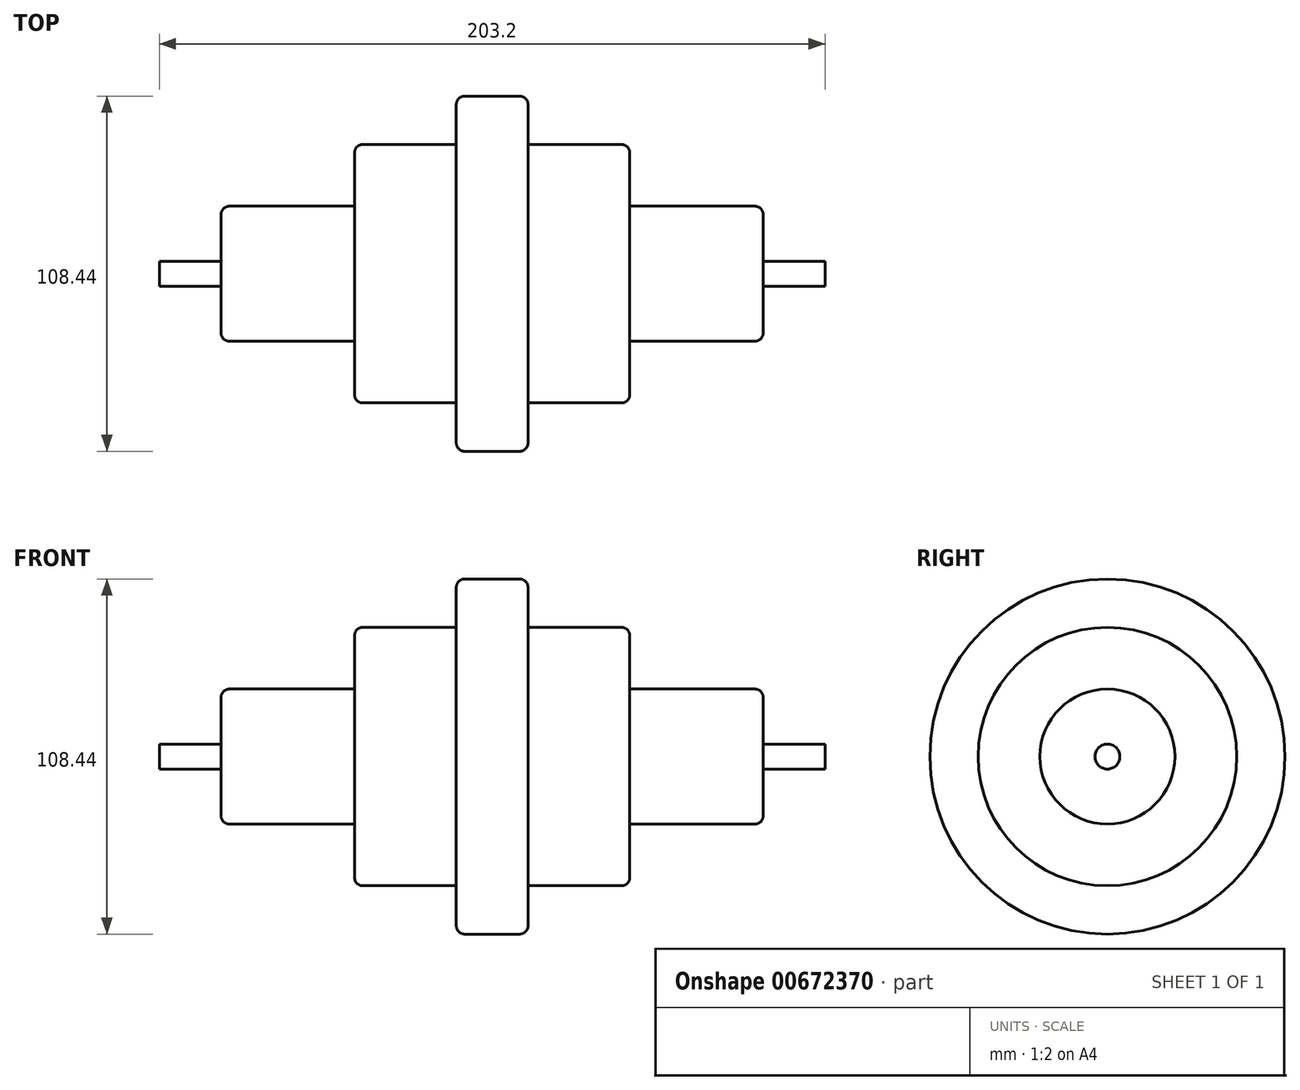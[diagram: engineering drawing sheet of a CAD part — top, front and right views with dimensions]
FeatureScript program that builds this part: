
annotation { "Feature Type Name" : "Feature", "Feature Type Description" : "" }
export const myFeature = defineFeature(function(context is Context, id is Id, definition is map)
    precondition{}
    {
        {
            var Q0;
            Q0=qCreatedBy(makeId("Right.planeOp"),FACE);
            var sketch = newSketch(context, id + "F0", { "sketchPlane" : qUnion([Q0])});
            skCircle(sketch, "E0", {"center": v(0, 0) * mm, "radius": 3.81 * mm});
            skSolve(sketch);
        }
        {
            var Q0;
            Q0=makeQuery(id+"F0.imprint","IMPRINT",FACE,{"disambiguationData":[TD([[makeQuery(id+"F0.imprint","IMPRINT",EDGE,{"derivedFrom":sQuery(id+"F0.wireOp",EDGE,"E0")}),1.0]])]});
            extrude(context, id + "F1", {"entities" : qUnion([Q0]), "endBound" : BoundingType.SYMMETRIC, "depth" : 203.2 * mm, "offsetDistance" : 25.4 * mm});
        }
        {
            var Q0;
            Q0=qCreatedBy(makeId("Front.planeOp"),FACE);
            var sketch = newSketch(context, id + "F2", { "sketchPlane" : qUnion([Q0])});
            skLineSegment(sketch, "E1", {"start": v(0, 0) * mm, "end": v(0, 54.22) * mm, "construction": true});
            skLineSegment(sketch, "E2", {"start": v(-82.74, 0) * mm, "end": v(-82.74, 20.62) * mm});
            skLineSegment(sketch, "E3", {"start": v(-82.74, 20.62) * mm, "end": v(-42, 20.62) * mm});
            skLineSegment(sketch, "E4", {"start": v(-42, 20.62) * mm, "end": v(-42, 39.46) * mm});
            skLineSegment(sketch, "E5", {"start": v(-42, 39.46) * mm, "end": v(-10.95, 39.46) * mm});
            skLineSegment(sketch, "E6", {"start": v(-10.95, 39.46) * mm, "end": v(-10.95, 54.22) * mm});
            skLineSegment(sketch, "E7", {"start": v(-10.95, 54.22) * mm, "end": v(0, 54.22) * mm});
            skLineSegment(sketch, "E8.MirrorCS", {"start": v(10.95, 54.22) * mm, "end": v(0, 54.22) * mm});
            skLineSegment(sketch, "E9.MirrorCS", {"start": v(82.74, 20.62) * mm, "end": v(42, 20.62) * mm});
            skLineSegment(sketch, "E10.MirrorCS", {"start": v(42, 39.46) * mm, "end": v(10.95, 39.46) * mm});
            skLineSegment(sketch, "E11.MirrorCS", {"start": v(82.74, 0) * mm, "end": v(82.74, 20.62) * mm});
            skLineSegment(sketch, "E12.MirrorCS", {"start": v(42, 20.62) * mm, "end": v(42, 39.46) * mm});
            skLineSegment(sketch, "E13.MirrorCS", {"start": v(10.95, 39.46) * mm, "end": v(10.95, 54.22) * mm});
            skLineSegment(sketch, "E14", {"start": v(-82.74, 0) * mm, "end": v(82.74, 0) * mm});
            skSolve(sketch);
        }
        {
            var Q0;
            Q0=makeQuery(id+"F2.imprint","IMPRINT",FACE,{"disambiguationData":[TD([[makeQuery(id+"F2.imprint","IMPRINT",EDGE,{"derivedFrom":sQuery(id+"F2.wireOp",EDGE,"E2")}),-1.0]])]});
            var Q1;
            Q1=sQuery(id+"F2.wireOp",EDGE,"E14");
            revolve(context, id + "F3", {"operationType" : NewBodyOperationType.ADD, "entities" : qUnion([Q0]), "axis" : qUnion([Q1]), "revolveType" : RevolveType.FULL});
        }
        {
            var Q0;
            Q0=makeQuery(id+"F3.opRevolve","SWEPT_EDGE",EDGE,{"disambiguationData":[OSD([sQuery(id+"F2.wireOp",EDGE,"E6"),sQuery(id+"F2.wireOp",EDGE,"E7")])]});
            var Q1;
            Q1=makeQuery(id+"F3.opRevolve","SWEPT_EDGE",EDGE,{"disambiguationData":[OSD([sQuery(id+"F2.wireOp",EDGE,"E4"),sQuery(id+"F2.wireOp",EDGE,"E5")])]});
            var Q2;
            Q2=makeQuery(id+"F3.opRevolve","SWEPT_EDGE",EDGE,{"disambiguationData":[OSD([sQuery(id+"F2.wireOp",EDGE,"E2"),sQuery(id+"F2.wireOp",EDGE,"E3")])]});
            var Q3;
            Q3=makeQuery(id+"F3.opRevolve","SWEPT_EDGE",EDGE,{"disambiguationData":[OSD([sQuery(id+"F2.wireOp",EDGE,"E8.MirrorCS"),sQuery(id+"F2.wireOp",EDGE,"E13.MirrorCS")])]});
            var Q4;
            Q4=makeQuery(id+"F3.opRevolve","SWEPT_EDGE",EDGE,{"disambiguationData":[OSD([sQuery(id+"F2.wireOp",EDGE,"E10.MirrorCS"),sQuery(id+"F2.wireOp",EDGE,"E12.MirrorCS")])]});
            var Q5;
            Q5=makeQuery(id+"F3.opRevolve","SWEPT_EDGE",EDGE,{"disambiguationData":[OSD([sQuery(id+"F2.wireOp",EDGE,"E9.MirrorCS"),sQuery(id+"F2.wireOp",EDGE,"E11.MirrorCS")])]});
            fillet(context, id + "F4", {"entities" : qUnion([Q0, Q1, Q2, Q3, Q4, Q5]), "radius" : 2.54 * mm, "tangentPropagation" : true, "allowEdgeOverflow" : false});
        }
    });
